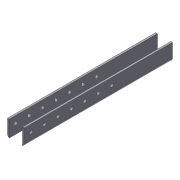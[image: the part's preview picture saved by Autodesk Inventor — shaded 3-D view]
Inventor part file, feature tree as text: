
AUTODESK INVENTOR PART (.ipt)
format: ipt  version: 2012 (Build 160160000, 160)  size: 137,216 bytes
history: native  units: in
note: dims shown in document units (in); Inventor stores cm internally (conversion verified against a paired STEP export)
features: extrude x4, sketch x4, pattern_linear x1
ambient origin geometry x8: Origin, YZ Plane, XZ Plane, XY Plane, X Axis, Y Axis, Z Axis, Center Point
bodies: Solid1 (feature_tree)
feature tree (9):
  extrude  "Extrusion1"  Depth=1.0in
  extrude  "Extrusion2"  Depth=0.125in
  pattern_linear  "Rectangular Pattern1"  Spacing1=0.5in  [1 undecoded]
  extrude  "Extrusion3"  Depth=0.5in
  extrude  "Extrusion4"  Depth=7.0in TaperAngle=0.0deg
  sketch  "Sketch1"  dims[d0=0.125in d1=1.0in]
  sketch  "Sketch2"  dims[d2=1.0in d3=0.125in]
  sketch  "Sketch3"  dims[d4=11.0in d5=0.0in]
  sketch  "Sketch4"  dims[d6=0.25in d7=0.5in d8=0.5in d9=7.0in d10=0.0in d11=2.7559in d13=1.0in d14=0.5in d15=2.0in d16=7.0in d17=0.0in d18=1.0in d19=1.125in d20=0.0in d21=0.0in d22=7.0in d23=0.0in]
note: 1 required parameter value undecoded (feature->parameter linkage not recoverable at this tier; creation-order binding heuristic only, values carry confidence <= 0.55)
